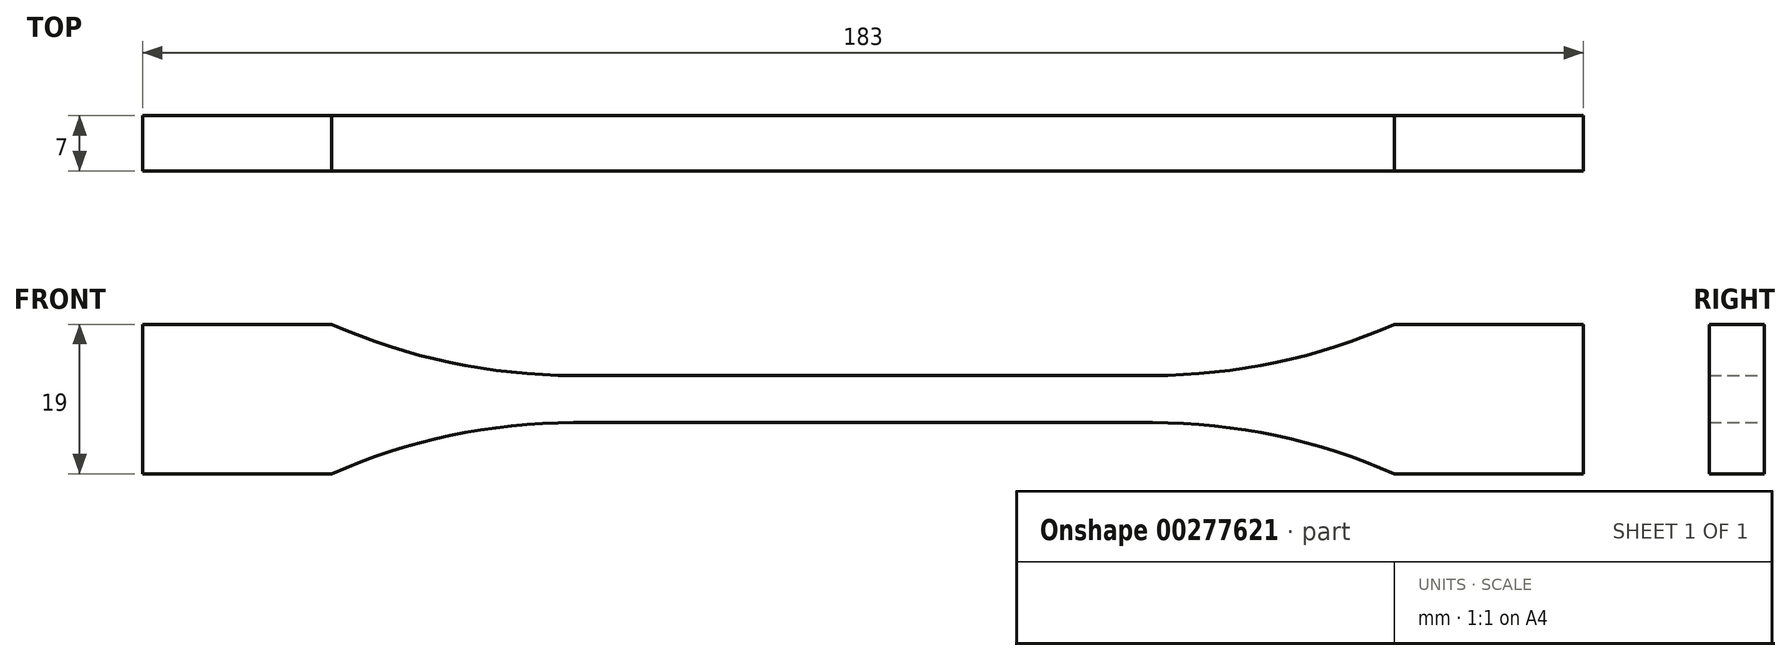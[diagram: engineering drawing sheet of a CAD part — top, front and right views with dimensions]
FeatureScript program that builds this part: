
annotation { "Feature Type Name" : "Feature", "Feature Type Description" : "" }
export const myFeature = defineFeature(function(context is Context, id is Id, definition is map)
    precondition{}
    {
        {
            var Q0;
            Q0=qCreatedBy(makeId("Front.planeOp"),FACE);
            var sketch = newSketch(context, id + "F0", { "sketchPlane" : qUnion([Q0])});
            skLineSegment(sketch, "E0", {"start": v(0, 3) * mm, "end": v(36.75, 3) * mm});
            skArc(sketch, "E1", {"start": v(36.75, 3) * mm, "mid": v(52.46, 4.64) * mm, "end": v(67.5, 9.5) * mm});
            skLineSegment(sketch, "E2", {"start": v(67.5, 9.5) * mm, "end": v(91.5, 9.5) * mm});
            skLineSegment(sketch, "E3.MirrorCS", {"start": v(0, -3) * mm, "end": v(36.75, -3) * mm});
            skLineSegment(sketch, "E4.MirrorCS", {"start": v(67.5, -9.5) * mm, "end": v(91.5, -9.5) * mm});
            skArc(sketch, "E5.MirrorCS", {"start": v(36.75, -3) * mm, "mid": v(52.46, -4.64) * mm, "end": v(67.5, -9.5) * mm});
            skLineSegment(sketch, "E6.MirrorCS", {"start": v(-67.5, -9.5) * mm, "end": v(-91.5, -9.5) * mm});
            skLineSegment(sketch, "E7.MirrorCS", {"start": v(0, -3) * mm, "end": v(-36.75, -3) * mm});
            skLineSegment(sketch, "E8.MirrorCS", {"start": v(0, 3) * mm, "end": v(-36.75, 3) * mm});
            skLineSegment(sketch, "E9.MirrorCS", {"start": v(-67.5, 9.5) * mm, "end": v(-91.5, 9.5) * mm});
            skArc(sketch, "E10.MirrorCS", {"start": v(-36.75, -3) * mm, "mid": v(-52.46, -4.64) * mm, "end": v(-67.5, -9.5) * mm});
            skArc(sketch, "E11.MirrorCS", {"start": v(-36.75, 3) * mm, "mid": v(-52.46, 4.64) * mm, "end": v(-67.5, 9.5) * mm});
            skLineSegment(sketch, "E12", {"start": v(-91.5, 9.5) * mm, "end": v(-91.5, -9.5) * mm});
            skLineSegment(sketch, "E13", {"start": v(91.5, 9.5) * mm, "end": v(91.5, -9.5) * mm});
            skSolve(sketch);
        }
        {
            var Q0;
            Q0 = qSketchRegion(id + "F0", true);
            extrude(context, id + "F1", {"entities" : qUnion([Q0]), "endBound" : BoundingType.SYMMETRIC, "depth" : 7 * mm});
        }
    });
